SOLIDWORKS PART (.sldprt)
format: sldprt  version: not decoded by parser v0  size: 224,768 bytes
history: native  units: mm
features: plane x3, sketch x2, extrude x2, material x1, chamfer x1, pattern_linear x1 (+8 scaffold rows collapsed)
feature tree (18):
  scaffold x8  (default folders/planes/origin — collapsed)
  material  "Material <not specified>"
  plane  "Alzado"
  plane  "Planta"
  plane  "Vista lateral"
  sketch  "Croquis1"  dims[D1=0.5mm D2=0.5mm]
  extrude  "Extruir1"  Depth=8.5mm
  sketch  "Croquis2"  dims[D1=2.54mm D2=2.54mm D3=1.27mm D4=1.27mm]
  extrude  "Extruir2"  Depth=2.2mm
  chamfer  "Chaflán1"  Distance=0.2mm Angle=45deg
  pattern_linear  "MatrizL1"  Count1=5 Count2=1 Spacing1=2.54mm Spacing2=1mm
decode coverage: 6 of 6 modeling features carry decoded parameters
note: suppression state not decoded; provenance and decode notes live in map.json
